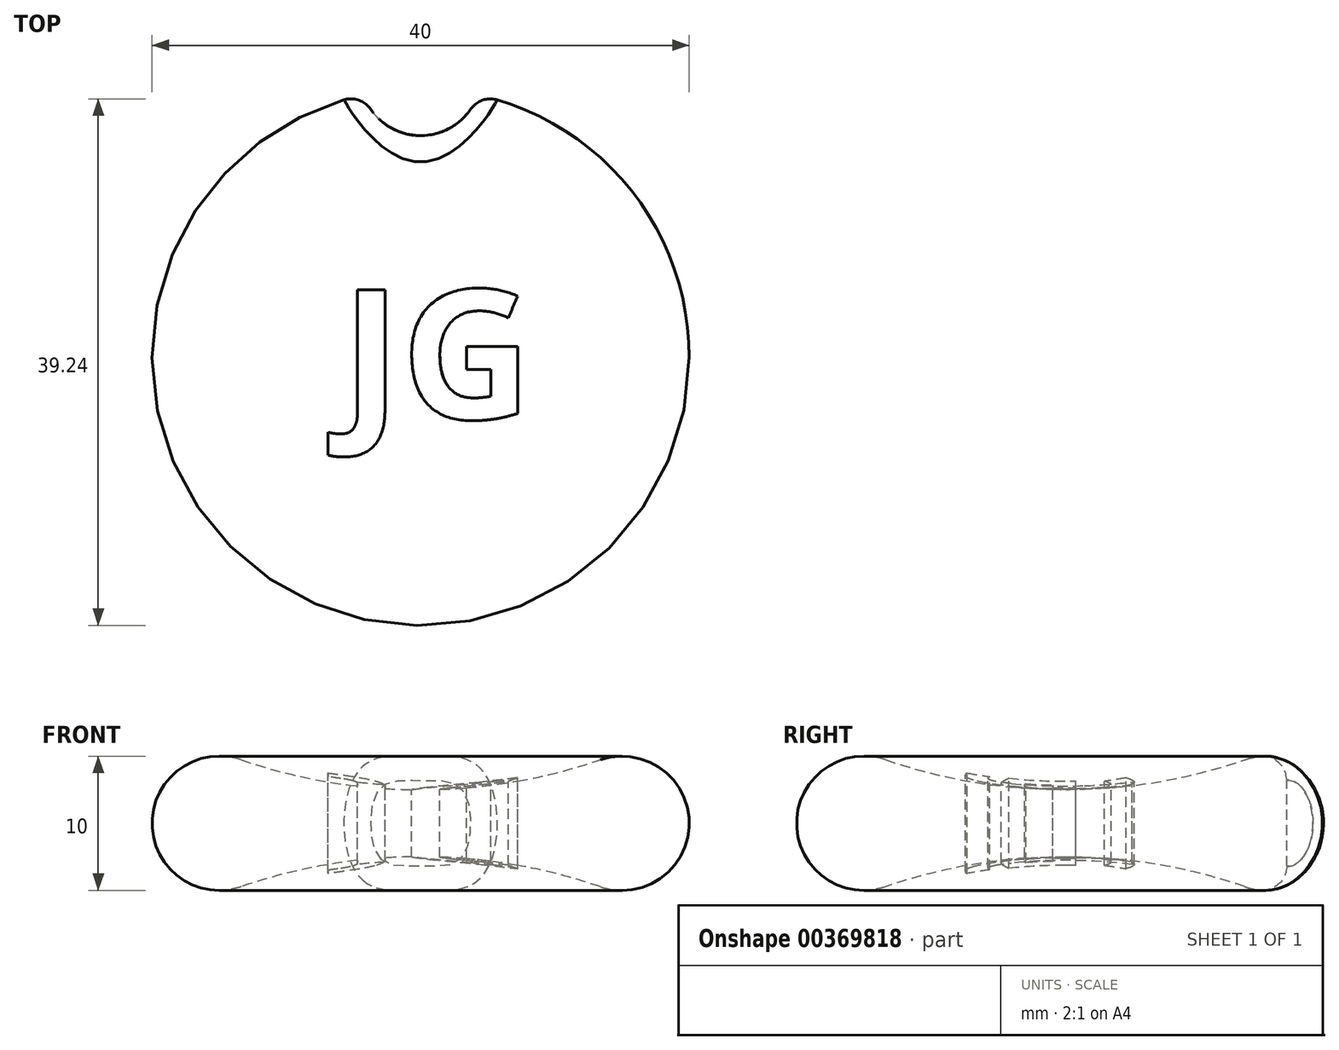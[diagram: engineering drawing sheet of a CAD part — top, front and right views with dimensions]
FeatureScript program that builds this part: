
annotation { "Feature Type Name" : "Feature", "Feature Type Description" : "" }
export const myFeature = defineFeature(function(context is Context, id is Id, definition is map)
    precondition{}
    {
        {
            var Q0;
            Q0=qCreatedBy(makeId("Front.planeOp"),FACE);
            var sketch = newSketch(context, id + "F0", { "sketchPlane" : qUnion([Q0])});
            skArc(sketch, "E0", {"start": v(-13.38, 4.73) * mm, "mid": v(-20, 0) * mm, "end": v(-13.38, -4.73) * mm});
            skArc(sketch, "E1", {"start": v(-13.38, 4.73) * mm, "mid": v(-6.78, 3.06) * mm, "end": v(0, 2.5) * mm});
            skArc(sketch, "E2", {"start": v(0, -2.5) * mm, "mid": v(-6.78, -3.06) * mm, "end": v(-13.38, -4.73) * mm});
            skLineSegment(sketch, "E3", {"start": v(0, 2.5) * mm, "end": v(0, -2.5) * mm});
            skSolve(sketch);
        }
        {
            var Q0;
            Q0 = qSketchRegion(id + "F0", true);
            var Q1;
            Q1=sQuery(id+"F0.wireOp",EDGE,"E3");
            revolve(context, id + "F1", {"entities" : qUnion([Q0]), "axis" : qUnion([Q1]), "revolveType" : RevolveType.FULL});
        }
        {
            var Q0;
            Q0=qCreatedBy(makeId("Top.planeOp"),FACE);
            cPlane(context, id + "F2", {"entities" : qUnion([Q0]), "cplaneType" : CPlaneType.OFFSET, "offset" : 5 * mm, "width" : 150 * mm, "height" : 150 * mm});
        }
        {
            var Q0;
            Q0=qCreatedBy(id+"F2.planeOp",FACE);
            var sketch = newSketch(context, id + "F3", { "sketchPlane" : qUnion([Q0])});
            skCircle(sketch, "E4", {"center": v(0, 21) * mm, "radius": 4.5 * mm});
            skSolve(sketch);
        }
        {
            var Q0;
            Q0 = qSketchRegion(id + "F3", true);
            extrude(context, id + "F4", {"entities" : qUnion([Q0]), "operationType" : NewBodyOperationType.REMOVE, "oppositeDirection" : true, "depth" : 10 * mm});
        }
        {
            var Q0;
            Q0=makeQuery(id+"F4.boolean.opBoolean","INTERSECT",EDGE,{"derivedFrom":[makeQuery(id+"F1.opRevolve","SWEPT_FACE",FACE,{"disambiguationData":[OSD([sQuery(id+"F0.wireOp",EDGE,"E0")])]}),makeQuery(id+"F4.opExtrude","SWEPT_FACE",FACE,{"disambiguationData":[OSD([sQuery(id+"F3.wireOp",EDGE,"E4")])]})]});
            fillet(context, id + "F5", {"entities" : qUnion([Q0]), "radius" : 1.8 * mm, "tangentPropagation" : true, "allowEdgeOverflow" : false});
        }
        {
            var Q0;
            Q0=qCreatedBy(id+"F2.planeOp",FACE);
            var sketch = newSketch(context, id + "F6", { "sketchPlane" : qUnion([Q0])});
            skText(sketch, "E5", { "text": "JG", "fontName": "OpenSans-Bold.ttf"});
            const initialGuessF6  = {"E5": [-0.00591, -0.00462, 1, 0, 0.0097]};
            skSetInitialGuess(sketch, initialGuessF6);
            skSolve(sketch);
        }
        {
            var Q0;
            Q0 = qSketchRegion(id + "F6", true);
            extrude(context, id + "F7", {"entities" : qUnion([Q0]), "operationType" : NewBodyOperationType.REMOVE, "oppositeDirection" : true, "depth" : 25 * mm});
        }
    });
